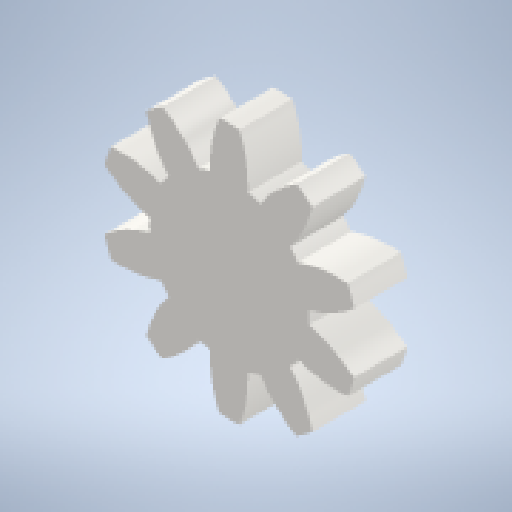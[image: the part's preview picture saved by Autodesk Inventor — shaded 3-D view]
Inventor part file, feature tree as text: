
AUTODESK INVENTOR PART (.ipt)
format: ipt  version: 2024 (Build 280153000, 153)  size: 222,208 bytes
history: native  units: mm (DEFAULTED — no unit token found)
features: plane x3, other x3, extrude x2, sketch x2
ambient origin geometry x8: Origin, YZ Plane, XZ Plane, XY Plane, X Axis, Y Axis, Z Axis, Center Point
bodies: Solid1 (feature_tree)
feature tree (10):
  extrude  "Extrusion1"  Depth=5.0mm TaperAngle=0.0deg
  plane  "Work Plane2"
  plane  "Work Plane8"
  plane  "Work Plane9"
  other  "Spur Gear"
  extrude  "Extrusion2"  Depth=10.0mm TaperAngle=0.0deg
  sketch  "Sketch1"  dims[d0=24.0mm d1=5.0mm d2=0.0mm]
  other  "Srf1"
  sketch  "Sketch3"  dims[d3=20.0mm d4=10.0mm d5=0.0mm d16=42.0mm d17=0.0mm d34=3.141593mm d39=0.0mm d41=0.0mm d43=42.0mm d46=42.0mm d47=0.0mm d48=0.0mm d49=3.0mm d50=10.0mm d51=0.0mm]
  other  "Pitch Diameter"
